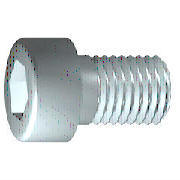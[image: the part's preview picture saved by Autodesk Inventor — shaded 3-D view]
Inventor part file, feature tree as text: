
AUTODESK INVENTOR PART (.ipt)
format: ipt  version: 2020 (Build 240168000, 168)  size: 192,512 bytes
history: native  units: mm (DEFAULTED — no unit token found)
features: sketch x2, extrude x1, plane x1, fillet x1
ambient origin geometry x7: Origin, YZ Plane, XY Plane, X Axis, Y Axis, Z Axis, Center Point
bodies: Solid1 (feature_tree), Body (feature_tree)
feature tree (5):
  extrude  "Slot"  Depth=2.0mm
  plane  "Work Plane1"
  fillet  "Fillet2"  Radius=2.0mm
  sketch  "Sketch1"  dims[d1=14.5mm d2=0.306825mm d3=2.0mm]
  sketch  "Sketch2"  dims[d4=1.5mm d5=60.0deg d6=3.0mm d7=3.0mm d8=2.309401mm d9=5.5mm d10=90.0deg d11=10.0mm d12=0.0mm d13=14.5mm d14=0.0mm d15=0.306725mm d16=0.306725mm d17=0.3mm d19=0.0mm d26=16.0mm d27=45.0deg d28=0.0mm d29=0.0mm d30=0.1mm]
